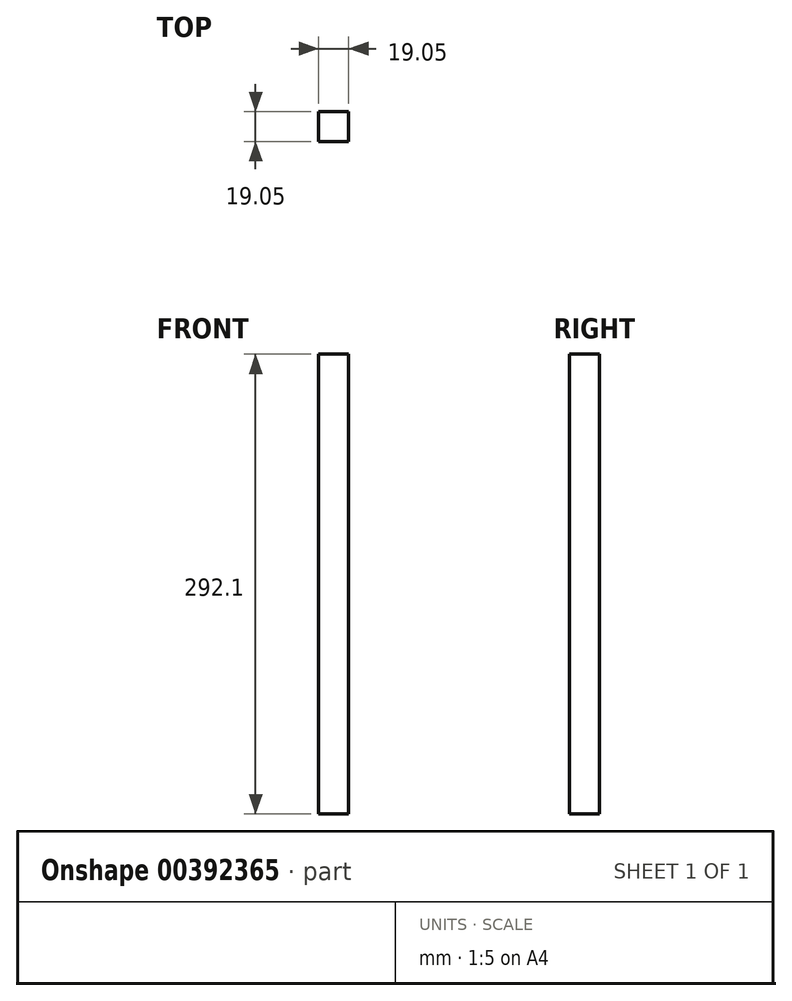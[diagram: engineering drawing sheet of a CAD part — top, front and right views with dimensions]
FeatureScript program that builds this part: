
annotation { "Feature Type Name" : "Feature", "Feature Type Description" : "" }
export const myFeature = defineFeature(function(context is Context, id is Id, definition is map)
    precondition{}
    {
        {
            var Q0;
            Q0=qCreatedBy(makeId("Front.planeOp"),FACE);
            var sketch = newSketch(context, id + "F0", { "sketchPlane" : qUnion([Q0])});
            skLineSegment(sketch, "E0.bottom", {"start": v(0, 0) * mm, "end": v(19.05, 0) * mm});
            skLineSegment(sketch, "E0.top", {"start": v(0, -292.1) * mm, "end": v(19.05, -292.1) * mm});
            skLineSegment(sketch, "E0.left", {"start": v(0, 0) * mm, "end": v(0, -292.1) * mm});
            skLineSegment(sketch, "E0.right", {"start": v(19.05, 0) * mm, "end": v(19.05, -292.1) * mm});
            skSolve(sketch);
        }
        {
            var Q0;
            Q0=makeQuery(id+"F0.imprint","IMPRINT",FACE,{"disambiguationData":[TD([[makeQuery(id+"F0.imprint","IMPRINT",EDGE,{"derivedFrom":sQuery(id+"F0.wireOp",EDGE,"E0.bottom")}),-1.0]])]});
            extrude(context, id + "F1", {"entities" : qUnion([Q0]), "depth" : 19.05 * mm});
        }
    });
